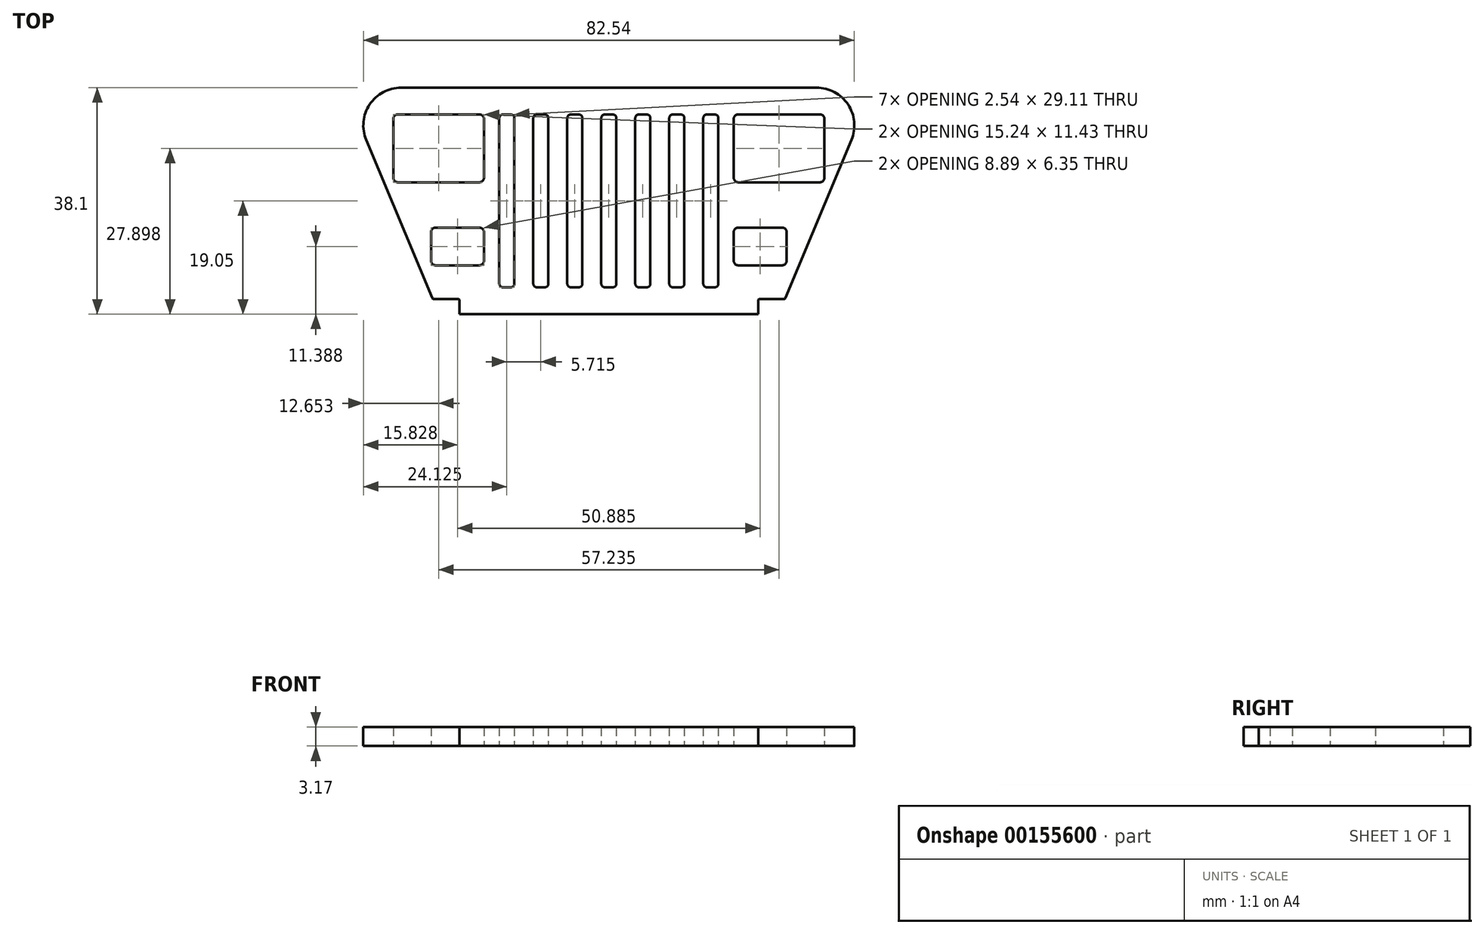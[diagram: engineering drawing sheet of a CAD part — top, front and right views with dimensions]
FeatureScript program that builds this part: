
annotation { "Feature Type Name" : "Feature", "Feature Type Description" : "" }
export const myFeature = defineFeature(function(context is Context, id is Id, definition is map)
    precondition{}
    {
        {
            var Q0;
            Q0=qCreatedBy(makeId("Top.planeOp"),FACE);
            var sketch = newSketch(context, id + "F0", { "sketchPlane" : qUnion([Q0])});
            skLineSegment(sketch, "E0.bottom", {"start": v(34.93, 19.05) * mm, "end": v(-0.14, 19.05) * mm});
            skLineSegment(sketch, "E0.top", {"start": v(25.1, -19.05) * mm, "end": v(-0.14, -19.05) * mm});
            skPoint(sketch, "E0.middle", {"position": v(0, 0) * mm});
            skLineSegment(sketch, "E1", {"start": v(-0.14, -19.05) * mm, "end": v(25.1, -19.05) * mm});
            skLineSegment(sketch, "E2", {"start": v(29.7, -16.35) * mm, "end": v(40.79, 10.26) * mm});
            skPoint(sketch, "E0.left.end.orphan", {"position": v(44.45, -19.05) * mm});
            skPoint(sketch, "E3.visualSharp", {"position": v(-44.45, 19.05) * mm});
            skPoint(sketch, "E4.visualSharp", {"position": v(44.45, 19.05) * mm});
            skArc(sketch, "E4.filletArc", {"start": v(40.79, 10.26) * mm, "mid": v(40.2, 16.22) * mm, "end": v(34.93, 19.05) * mm});
            skLineSegment(sketch, "E5", {"start": v(25.1, -19.05) * mm, "end": v(25.1, -16.76) * mm});
            skLineSegment(sketch, "E6", {"start": v(25.35, -16.5) * mm, "end": v(29.46, -16.5) * mm});
            skPoint(sketch, "E7.visualSharp", {"position": v(25.1, -16.5) * mm});
            skArc(sketch, "E7.filletArc", {"start": v(25.35, -16.51) * mm, "mid": v(25.17, -16.58) * mm, "end": v(25.1, -16.76) * mm});
            skPoint(sketch, "E8.visualSharp", {"position": v(29.63, -16.5) * mm});
            skArc(sketch, "E8.filletArc", {"start": v(29.46, -16.5) * mm, "mid": v(29.6, -16.47) * mm, "end": v(29.7, -16.35) * mm});
            skLineSegment(sketch, "E9", {"start": v(0, 30.6) * mm, "end": v(0, -24.02) * mm, "construction": true});
            skPoint(sketch, "E10", {"position": v(-0.14, 19.05) * mm});
            skPoint(sketch, "E11", {"position": v(-0.14, -19.05) * mm});
            skPoint(sketch, "E3.filletArc.start.orphan", {"position": v(-35.2, 19.05) * mm});
            skArc(sketch, "E12.MirrorCS", {"start": v(-25.35, -16.51) * mm, "mid": v(-25.17, -16.58) * mm, "end": v(-25.1, -16.76) * mm});
            skArc(sketch, "E13.MirrorCS", {"start": v(-29.46, -16.5) * mm, "mid": v(-29.6, -16.47) * mm, "end": v(-29.7, -16.35) * mm});
            skLineSegment(sketch, "E14.MirrorCS", {"start": v(-25.1, -19.05) * mm, "end": v(-25.1, -16.76) * mm});
            skLineSegment(sketch, "E15.MirrorCS", {"start": v(-25.1, -19.05) * mm, "end": v(0.14, -19.05) * mm});
            skLineSegment(sketch, "E16.MirrorCS", {"start": v(-25.35, -16.5) * mm, "end": v(-29.46, -16.5) * mm});
            skPoint(sketch, "E17.MirrorP", {"position": v(-44.45, -19.05) * mm});
            skLineSegment(sketch, "E18.MirrorCS", {"start": v(-29.7, -16.35) * mm, "end": v(-40.79, 10.26) * mm});
            skLineSegment(sketch, "E19.MirrorCS", {"start": v(0.14, -19.05) * mm, "end": v(-25.1, -19.05) * mm});
            skArc(sketch, "E20.MirrorCS", {"start": v(-40.79, 10.26) * mm, "mid": v(-40.2, 16.22) * mm, "end": v(-34.93, 19.05) * mm});
            skPoint(sketch, "E21.MirrorP", {"position": v(0.14, 19.05) * mm});
            skPoint(sketch, "E22.MirrorP", {"position": v(0.14, -19.05) * mm});
            skPoint(sketch, "E23.MirrorP", {"position": v(-25.1, -16.5) * mm});
            skLineSegment(sketch, "E24.MirrorCS", {"start": v(-34.93, 19.05) * mm, "end": v(0.14, 19.05) * mm});
            skPoint(sketch, "E25.MirrorP", {"position": v(-29.63, -16.5) * mm});
            skLineSegment(sketch, "E26.bottom", {"start": v(0.64, 14.55) * mm, "end": v(-0.64, 14.55) * mm});
            skLineSegment(sketch, "E26.top", {"start": v(0.64, -14.55) * mm, "end": v(-0.64, -14.55) * mm});
            skLineSegment(sketch, "E26.left", {"start": v(1.27, 13.92) * mm, "end": v(1.27, -13.92) * mm});
            skLineSegment(sketch, "E26.right", {"start": v(-1.27, 13.92) * mm, "end": v(-1.27, -13.92) * mm});
            skPoint(sketch, "E27.visualSharp", {"position": v(-1.27, 14.55) * mm});
            skArc(sketch, "E27.filletArc", {"start": v(-0.64, 14.55) * mm, "mid": v(-1.08, 14.37) * mm, "end": v(-1.27, 13.92) * mm});
            skPoint(sketch, "E28.visualSharp", {"position": v(1.27, 14.55) * mm});
            skArc(sketch, "E28.filletArc", {"start": v(1.27, 13.92) * mm, "mid": v(1.08, 14.37) * mm, "end": v(0.64, 14.55) * mm});
            skPoint(sketch, "E29.visualSharp", {"position": v(1.27, -14.55) * mm});
            skArc(sketch, "E29.filletArc", {"start": v(0.64, -14.55) * mm, "mid": v(1.08, -14.37) * mm, "end": v(1.27, -13.92) * mm});
            skPoint(sketch, "E30.visualSharp", {"position": v(-1.27, -14.55) * mm});
            skArc(sketch, "E30.filletArc", {"start": v(-1.27, -13.92) * mm, "mid": v(-1.08, -14.37) * mm, "end": v(-0.64, -14.55) * mm});
            skPoint(sketch, "E31.1.0.0", {"position": v(5.72, 0) * mm});
            skPoint(sketch, "E31.1.0.1", {"position": v(6.99, -14.55) * mm});
            skLineSegment(sketch, "E31.1.0.2", {"start": v(6.99, 13.92) * mm, "end": v(6.99, -13.92) * mm});
            skLineSegment(sketch, "E31.1.0.3", {"start": v(4.45, 13.92) * mm, "end": v(4.45, -13.92) * mm});
            skPoint(sketch, "E31.1.0.4", {"position": v(4.45, -14.55) * mm});
            skPoint(sketch, "E31.1.0.5", {"position": v(4.45, 14.55) * mm});
            skPoint(sketch, "E31.1.0.6", {"position": v(6.99, 14.55) * mm});
            skPoint(sketch, "E31.1.0.7", {"position": v(5.86, 19.05) * mm});
            skPoint(sketch, "E31.1.0.8", {"position": v(5.72, 0) * mm});
            skPoint(sketch, "E31.1.0.9", {"position": v(5.86, -19.05) * mm});
            skPoint(sketch, "E31.1.0.10", {"position": v(5.72, 0) * mm});
            skPoint(sketch, "E31.1.0.11", {"position": v(5.57, -19.05) * mm});
            skArc(sketch, "E31.1.0.12", {"start": v(6.99, 13.92) * mm, "mid": v(6.8, 14.37) * mm, "end": v(6.35, 14.55) * mm});
            skArc(sketch, "E31.1.0.13", {"start": v(4.45, -13.92) * mm, "mid": v(4.63, -14.37) * mm, "end": v(5.08, -14.55) * mm});
            skArc(sketch, "E31.1.0.14", {"start": v(5.08, 14.55) * mm, "mid": v(4.63, 14.37) * mm, "end": v(4.45, 13.92) * mm});
            skLineSegment(sketch, "E31.1.0.15", {"start": v(6.35, 14.55) * mm, "end": v(5.08, 14.55) * mm});
            skArc(sketch, "E31.1.0.16", {"start": v(6.35, -14.55) * mm, "mid": v(6.8, -14.37) * mm, "end": v(6.99, -13.92) * mm});
            skLineSegment(sketch, "E31.1.0.17", {"start": v(6.35, -14.55) * mm, "end": v(5.08, -14.55) * mm});
            skPoint(sketch, "E31.2.0.0", {"position": v(11.43, 0) * mm});
            skPoint(sketch, "E31.2.0.1", {"position": v(12.7, -14.55) * mm});
            skLineSegment(sketch, "E31.2.0.2", {"start": v(12.7, 13.92) * mm, "end": v(12.7, -13.92) * mm});
            skLineSegment(sketch, "E31.2.0.3", {"start": v(10.16, 13.92) * mm, "end": v(10.16, -13.92) * mm});
            skPoint(sketch, "E31.2.0.4", {"position": v(10.16, -14.55) * mm});
            skPoint(sketch, "E31.2.0.5", {"position": v(10.16, 14.55) * mm});
            skPoint(sketch, "E31.2.0.6", {"position": v(12.7, 14.55) * mm});
            skPoint(sketch, "E31.2.0.7", {"position": v(11.57, 19.05) * mm});
            skPoint(sketch, "E31.2.0.8", {"position": v(11.43, 0) * mm});
            skPoint(sketch, "E31.2.0.9", {"position": v(11.57, -19.05) * mm});
            skPoint(sketch, "E31.2.0.10", {"position": v(11.43, 0) * mm});
            skPoint(sketch, "E31.2.0.11", {"position": v(11.29, -19.05) * mm});
            skArc(sketch, "E31.2.0.12", {"start": v(12.7, 13.92) * mm, "mid": v(12.51, 14.37) * mm, "end": v(12.07, 14.55) * mm});
            skArc(sketch, "E31.2.0.13", {"start": v(10.16, -13.92) * mm, "mid": v(10.35, -14.37) * mm, "end": v(10.8, -14.55) * mm});
            skArc(sketch, "E31.2.0.14", {"start": v(10.8, 14.55) * mm, "mid": v(10.35, 14.37) * mm, "end": v(10.16, 13.92) * mm});
            skLineSegment(sketch, "E31.2.0.15", {"start": v(12.07, 14.55) * mm, "end": v(10.8, 14.55) * mm});
            skArc(sketch, "E31.2.0.16", {"start": v(12.07, -14.55) * mm, "mid": v(12.51, -14.37) * mm, "end": v(12.7, -13.92) * mm});
            skLineSegment(sketch, "E31.2.0.17", {"start": v(12.07, -14.55) * mm, "end": v(10.8, -14.55) * mm});
            skPoint(sketch, "E31.3.0.0", {"position": v(17.14, 0) * mm});
            skPoint(sketch, "E31.3.0.1", {"position": v(18.41, -14.55) * mm});
            skLineSegment(sketch, "E31.3.0.2", {"start": v(18.41, 13.92) * mm, "end": v(18.41, -13.92) * mm});
            skLineSegment(sketch, "E31.3.0.3", {"start": v(15.88, 13.92) * mm, "end": v(15.88, -13.92) * mm});
            skPoint(sketch, "E31.3.0.4", {"position": v(15.88, -14.55) * mm});
            skPoint(sketch, "E31.3.0.5", {"position": v(15.88, 14.55) * mm});
            skPoint(sketch, "E31.3.0.6", {"position": v(18.41, 14.55) * mm});
            skPoint(sketch, "E31.3.0.7", {"position": v(17.29, 19.05) * mm});
            skPoint(sketch, "E31.3.0.8", {"position": v(17.14, 0) * mm});
            skPoint(sketch, "E31.3.0.9", {"position": v(17.29, -19.05) * mm});
            skPoint(sketch, "E31.3.0.10", {"position": v(17.14, 0) * mm});
            skPoint(sketch, "E31.3.0.11", {"position": v(17, -19.05) * mm});
            skArc(sketch, "E31.3.0.12", {"start": v(18.41, 13.92) * mm, "mid": v(18.23, 14.37) * mm, "end": v(17.78, 14.55) * mm});
            skArc(sketch, "E31.3.0.13", {"start": v(15.88, -13.92) * mm, "mid": v(16.06, -14.37) * mm, "end": v(16.51, -14.55) * mm});
            skArc(sketch, "E31.3.0.14", {"start": v(16.51, 14.55) * mm, "mid": v(16.06, 14.37) * mm, "end": v(15.88, 13.92) * mm});
            skLineSegment(sketch, "E31.3.0.15", {"start": v(17.78, 14.55) * mm, "end": v(16.51, 14.55) * mm});
            skArc(sketch, "E31.3.0.16", {"start": v(17.78, -14.55) * mm, "mid": v(18.23, -14.37) * mm, "end": v(18.41, -13.92) * mm});
            skLineSegment(sketch, "E31.3.0.17", {"start": v(17.78, -14.55) * mm, "end": v(16.51, -14.55) * mm});
            skLineSegment(sketch, "E31.direction1", {"start": v(0.14, -19.05) * mm, "end": v(5.86, -19.05) * mm, "construction": true});
            skPoint(sketch, "E32.1.0.0", {"position": v(-4.44, -14.55) * mm});
            skLineSegment(sketch, "E32.1.0.1", {"start": v(-6.99, 13.92) * mm, "end": v(-6.99, -13.92) * mm});
            skPoint(sketch, "E32.1.0.2", {"position": v(-6.99, -14.55) * mm});
            skLineSegment(sketch, "E32.1.0.3", {"start": v(-4.44, 13.92) * mm, "end": v(-4.44, -13.92) * mm});
            skPoint(sketch, "E32.1.0.4", {"position": v(-5.72, 0) * mm});
            skPoint(sketch, "E32.1.0.5", {"position": v(-6.99, 14.55) * mm});
            skPoint(sketch, "E32.1.0.6", {"position": v(-5.72, 0) * mm});
            skPoint(sketch, "E32.1.0.7", {"position": v(-4.44, 14.55) * mm});
            skPoint(sketch, "E32.1.0.8", {"position": v(-5.86, -19.05) * mm});
            skPoint(sketch, "E32.1.0.9", {"position": v(-5.72, 0) * mm});
            skPoint(sketch, "E32.1.0.10", {"position": v(-5.57, -19.05) * mm});
            skPoint(sketch, "E32.1.0.11", {"position": v(-5.86, 19.05) * mm});
            skLineSegment(sketch, "E32.1.0.12", {"start": v(-5.08, -14.55) * mm, "end": v(-6.35, -14.55) * mm});
            skArc(sketch, "E32.1.0.13", {"start": v(-6.99, -13.92) * mm, "mid": v(-6.8, -14.37) * mm, "end": v(-6.35, -14.55) * mm});
            skArc(sketch, "E32.1.0.14", {"start": v(-5.08, -14.55) * mm, "mid": v(-4.63, -14.37) * mm, "end": v(-4.44, -13.92) * mm});
            skLineSegment(sketch, "E32.1.0.15", {"start": v(-5.08, 14.55) * mm, "end": v(-6.35, 14.55) * mm});
            skArc(sketch, "E32.1.0.16", {"start": v(-6.35, 14.55) * mm, "mid": v(-6.8, 14.37) * mm, "end": v(-6.99, 13.92) * mm});
            skArc(sketch, "E32.1.0.17", {"start": v(-4.44, 13.92) * mm, "mid": v(-4.63, 14.37) * mm, "end": v(-5.08, 14.55) * mm});
            skPoint(sketch, "E32.1.0.18", {"position": v(-5.57, 19.05) * mm});
            skPoint(sketch, "E32.2.0.0", {"position": v(-10.16, -14.55) * mm});
            skLineSegment(sketch, "E32.2.0.1", {"start": v(-12.7, 13.92) * mm, "end": v(-12.7, -13.92) * mm});
            skPoint(sketch, "E32.2.0.2", {"position": v(-12.7, -14.55) * mm});
            skLineSegment(sketch, "E32.2.0.3", {"start": v(-10.16, 13.92) * mm, "end": v(-10.16, -13.92) * mm});
            skPoint(sketch, "E32.2.0.4", {"position": v(-11.43, 0) * mm});
            skPoint(sketch, "E32.2.0.5", {"position": v(-12.7, 14.55) * mm});
            skPoint(sketch, "E32.2.0.6", {"position": v(-11.43, 0) * mm});
            skPoint(sketch, "E32.2.0.7", {"position": v(-10.16, 14.55) * mm});
            skPoint(sketch, "E32.2.0.8", {"position": v(-11.57, -19.05) * mm});
            skPoint(sketch, "E32.2.0.9", {"position": v(-11.43, 0) * mm});
            skPoint(sketch, "E32.2.0.10", {"position": v(-11.29, -19.05) * mm});
            skPoint(sketch, "E32.2.0.11", {"position": v(-11.57, 19.05) * mm});
            skLineSegment(sketch, "E32.2.0.12", {"start": v(-10.8, -14.55) * mm, "end": v(-12.07, -14.55) * mm});
            skArc(sketch, "E32.2.0.13", {"start": v(-12.7, -13.92) * mm, "mid": v(-12.51, -14.37) * mm, "end": v(-12.07, -14.55) * mm});
            skArc(sketch, "E32.2.0.14", {"start": v(-10.8, -14.55) * mm, "mid": v(-10.35, -14.37) * mm, "end": v(-10.16, -13.92) * mm});
            skLineSegment(sketch, "E32.2.0.15", {"start": v(-10.8, 14.55) * mm, "end": v(-12.07, 14.55) * mm});
            skArc(sketch, "E32.2.0.16", {"start": v(-12.07, 14.55) * mm, "mid": v(-12.51, 14.37) * mm, "end": v(-12.7, 13.92) * mm});
            skArc(sketch, "E32.2.0.17", {"start": v(-10.16, 13.92) * mm, "mid": v(-10.35, 14.37) * mm, "end": v(-10.8, 14.55) * mm});
            skPoint(sketch, "E32.2.0.18", {"position": v(-11.29, 19.05) * mm});
            skPoint(sketch, "E32.3.0.0", {"position": v(-15.88, -14.55) * mm});
            skLineSegment(sketch, "E32.3.0.1", {"start": v(-18.42, 13.92) * mm, "end": v(-18.42, -13.92) * mm});
            skPoint(sketch, "E32.3.0.2", {"position": v(-18.42, -14.55) * mm});
            skLineSegment(sketch, "E32.3.0.3", {"start": v(-15.88, 13.92) * mm, "end": v(-15.88, -13.92) * mm});
            skPoint(sketch, "E32.3.0.4", {"position": v(-17.15, 0) * mm});
            skPoint(sketch, "E32.3.0.5", {"position": v(-18.42, 14.55) * mm});
            skPoint(sketch, "E32.3.0.6", {"position": v(-17.15, 0) * mm});
            skPoint(sketch, "E32.3.0.7", {"position": v(-15.88, 14.55) * mm});
            skPoint(sketch, "E32.3.0.8", {"position": v(-17.29, -19.05) * mm});
            skPoint(sketch, "E32.3.0.9", {"position": v(-17.15, 0) * mm});
            skPoint(sketch, "E32.3.0.10", {"position": v(-17, -19.05) * mm});
            skPoint(sketch, "E32.3.0.11", {"position": v(-17.29, 19.05) * mm});
            skLineSegment(sketch, "E32.3.0.12", {"start": v(-16.51, -14.55) * mm, "end": v(-17.78, -14.55) * mm});
            skArc(sketch, "E32.3.0.13", {"start": v(-18.42, -13.92) * mm, "mid": v(-18.23, -14.37) * mm, "end": v(-17.78, -14.55) * mm});
            skArc(sketch, "E32.3.0.14", {"start": v(-16.51, -14.55) * mm, "mid": v(-16.06, -14.37) * mm, "end": v(-15.88, -13.92) * mm});
            skLineSegment(sketch, "E32.3.0.15", {"start": v(-16.51, 14.55) * mm, "end": v(-17.78, 14.55) * mm});
            skArc(sketch, "E32.3.0.16", {"start": v(-17.78, 14.55) * mm, "mid": v(-18.23, 14.37) * mm, "end": v(-18.42, 13.92) * mm});
            skArc(sketch, "E32.3.0.17", {"start": v(-15.88, 13.92) * mm, "mid": v(-16.06, 14.37) * mm, "end": v(-16.51, 14.55) * mm});
            skPoint(sketch, "E32.3.0.18", {"position": v(-17, 19.05) * mm});
            skLineSegment(sketch, "E32.direction1", {"start": v(-0.14, -19.05) * mm, "end": v(-5.86, -19.05) * mm, "construction": true});
            skLineSegment(sketch, "E33.bottom", {"start": v(-35.48, 3.13) * mm, "end": v(-21.76, 3.13) * mm});
            skLineSegment(sketch, "E33.top", {"start": v(-35.48, 14.56) * mm, "end": v(-21.76, 14.56) * mm});
            skLineSegment(sketch, "E33.left", {"start": v(-36.24, 3.9) * mm, "end": v(-36.24, 13.8) * mm});
            skLineSegment(sketch, "E33.right", {"start": v(-21, 3.9) * mm, "end": v(-21, 13.8) * mm});
            skLineSegment(sketch, "E34.MirrorCS", {"start": v(35.48, 14.56) * mm, "end": v(21.76, 14.56) * mm});
            skLineSegment(sketch, "E35.MirrorCS", {"start": v(21, 3.9) * mm, "end": v(21, 13.8) * mm});
            skLineSegment(sketch, "E36.MirrorCS", {"start": v(36.24, 3.9) * mm, "end": v(36.24, 13.8) * mm});
            skLineSegment(sketch, "E37.MirrorCS", {"start": v(35.48, 3.13) * mm, "end": v(21.76, 3.13) * mm});
            skLineSegment(sketch, "E38.bottom", {"start": v(-29.13, -10.84) * mm, "end": v(-21.76, -10.84) * mm});
            skLineSegment(sketch, "E38.top", {"start": v(-29.13, -4.49) * mm, "end": v(-21.76, -4.49) * mm});
            skLineSegment(sketch, "E38.left", {"start": v(-29.89, -10.07) * mm, "end": v(-29.89, -5.25) * mm});
            skLineSegment(sketch, "E38.right", {"start": v(-21, -10.07) * mm, "end": v(-21, -5.25) * mm});
            skLineSegment(sketch, "E39.MirrorCS", {"start": v(29.13, -4.49) * mm, "end": v(21.76, -4.49) * mm});
            skLineSegment(sketch, "E40.MirrorCS", {"start": v(29.89, -10.07) * mm, "end": v(29.89, -5.25) * mm});
            skLineSegment(sketch, "E41.MirrorCS", {"start": v(21, -10.07) * mm, "end": v(21, -5.25) * mm});
            skLineSegment(sketch, "E42.MirrorCS", {"start": v(29.13, -10.84) * mm, "end": v(21.76, -10.84) * mm});
            skPoint(sketch, "E43", {"position": v(-32.86, -8.78) * mm});
            skPoint(sketch, "E44.visualSharp", {"position": v(-36.24, 14.56) * mm});
            skArc(sketch, "E44.filletArc", {"start": v(-35.48, 14.56) * mm, "mid": v(-36.01, 14.34) * mm, "end": v(-36.24, 13.8) * mm});
            skPoint(sketch, "E45.visualSharp", {"position": v(-21, 14.56) * mm});
            skArc(sketch, "E45.filletArc", {"start": v(-21, 13.8) * mm, "mid": v(-21.22, 14.34) * mm, "end": v(-21.76, 14.56) * mm});
            skPoint(sketch, "E46.visualSharp", {"position": v(-21, 3.13) * mm});
            skArc(sketch, "E46.filletArc", {"start": v(-21.76, 3.13) * mm, "mid": v(-21.22, 3.36) * mm, "end": v(-21, 3.9) * mm});
            skPoint(sketch, "E47.visualSharp", {"position": v(-36.24, 3.13) * mm});
            skArc(sketch, "E47.filletArc", {"start": v(-36.24, 3.9) * mm, "mid": v(-36.01, 3.36) * mm, "end": v(-35.48, 3.13) * mm});
            skPoint(sketch, "E48.visualSharp", {"position": v(-29.89, -4.49) * mm});
            skArc(sketch, "E48.filletArc", {"start": v(-29.13, -4.49) * mm, "mid": v(-29.66, -4.7) * mm, "end": v(-29.89, -5.25) * mm});
            skPoint(sketch, "E49.visualSharp", {"position": v(-21, -4.49) * mm});
            skArc(sketch, "E49.filletArc", {"start": v(-21, -5.25) * mm, "mid": v(-21.22, -4.7) * mm, "end": v(-21.76, -4.49) * mm});
            skPoint(sketch, "E50.visualSharp", {"position": v(-21, -10.84) * mm});
            skArc(sketch, "E50.filletArc", {"start": v(-21.76, -10.84) * mm, "mid": v(-21.22, -10.61) * mm, "end": v(-21, -10.07) * mm});
            skPoint(sketch, "E51.visualSharp", {"position": v(-29.89, -10.84) * mm});
            skArc(sketch, "E51.filletArc", {"start": v(-29.89, -10.07) * mm, "mid": v(-29.66, -10.61) * mm, "end": v(-29.13, -10.84) * mm});
            skPoint(sketch, "E52.visualSharp", {"position": v(21, 14.56) * mm});
            skArc(sketch, "E52.filletArc", {"start": v(21.76, 14.56) * mm, "mid": v(21.22, 14.34) * mm, "end": v(21, 13.8) * mm});
            skPoint(sketch, "E53.visualSharp", {"position": v(36.24, 14.56) * mm});
            skArc(sketch, "E53.filletArc", {"start": v(36.24, 13.8) * mm, "mid": v(36.01, 14.34) * mm, "end": v(35.48, 14.56) * mm});
            skPoint(sketch, "E54.visualSharp", {"position": v(36.24, 3.13) * mm});
            skArc(sketch, "E54.filletArc", {"start": v(35.48, 3.13) * mm, "mid": v(36.01, 3.36) * mm, "end": v(36.24, 3.9) * mm});
            skPoint(sketch, "E55.visualSharp", {"position": v(21, 3.13) * mm});
            skArc(sketch, "E55.filletArc", {"start": v(21, 3.9) * mm, "mid": v(21.22, 3.36) * mm, "end": v(21.76, 3.13) * mm});
            skPoint(sketch, "E56.visualSharp", {"position": v(21, -4.49) * mm});
            skArc(sketch, "E56.filletArc", {"start": v(21.76, -4.49) * mm, "mid": v(21.22, -4.7) * mm, "end": v(21, -5.25) * mm});
            skPoint(sketch, "E57.visualSharp", {"position": v(29.89, -4.49) * mm});
            skArc(sketch, "E57.filletArc", {"start": v(29.89, -5.25) * mm, "mid": v(29.66, -4.7) * mm, "end": v(29.13, -4.49) * mm});
            skPoint(sketch, "E58.visualSharp", {"position": v(29.89, -10.84) * mm});
            skArc(sketch, "E58.filletArc", {"start": v(29.13, -10.84) * mm, "mid": v(29.66, -10.61) * mm, "end": v(29.89, -10.07) * mm});
            skPoint(sketch, "E59.visualSharp", {"position": v(21, -10.84) * mm});
            skArc(sketch, "E59.filletArc", {"start": v(21, -10.07) * mm, "mid": v(21.22, -10.61) * mm, "end": v(21.76, -10.84) * mm});
            skSolve(sketch);
        }
        {
            var Q0;
            Q0 = qSketchRegion(id + "F0", true);
            extrude(context, id + "F1", {"entities" : qUnion([Q0]), "flatOperationType" : FlatOperationType.REMOVE, "offsetDistance" : 25.4 * mm, "depth" : 3.17 * mm, "domain" : OperationDomain.MODEL});
        }
    });
